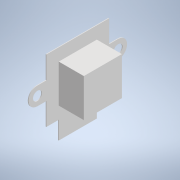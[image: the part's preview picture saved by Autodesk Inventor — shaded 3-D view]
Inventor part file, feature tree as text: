
AUTODESK INVENTOR PART (.ipt)
format: ipt  version: 2022 (Build 260153000, 153)  size: 130,560 bytes
history: native  units: mm
features: extrude x2, sketch x2, other x1
ambient origin geometry x8: Origin, YZ Plane, XZ Plane, XY Plane, X Axis, Y Axis, Z Axis, Center Point
bodies: Body1 (feature_tree)
feature tree (5):
  other  "Твердое тело1"
  extrude  "Выдавливание1"  Depth=14.0mm
  extrude  "Выдавливание2"  Depth=14.0mm
  sketch  "Эскиз1"
  sketch  "Эскиз2"
